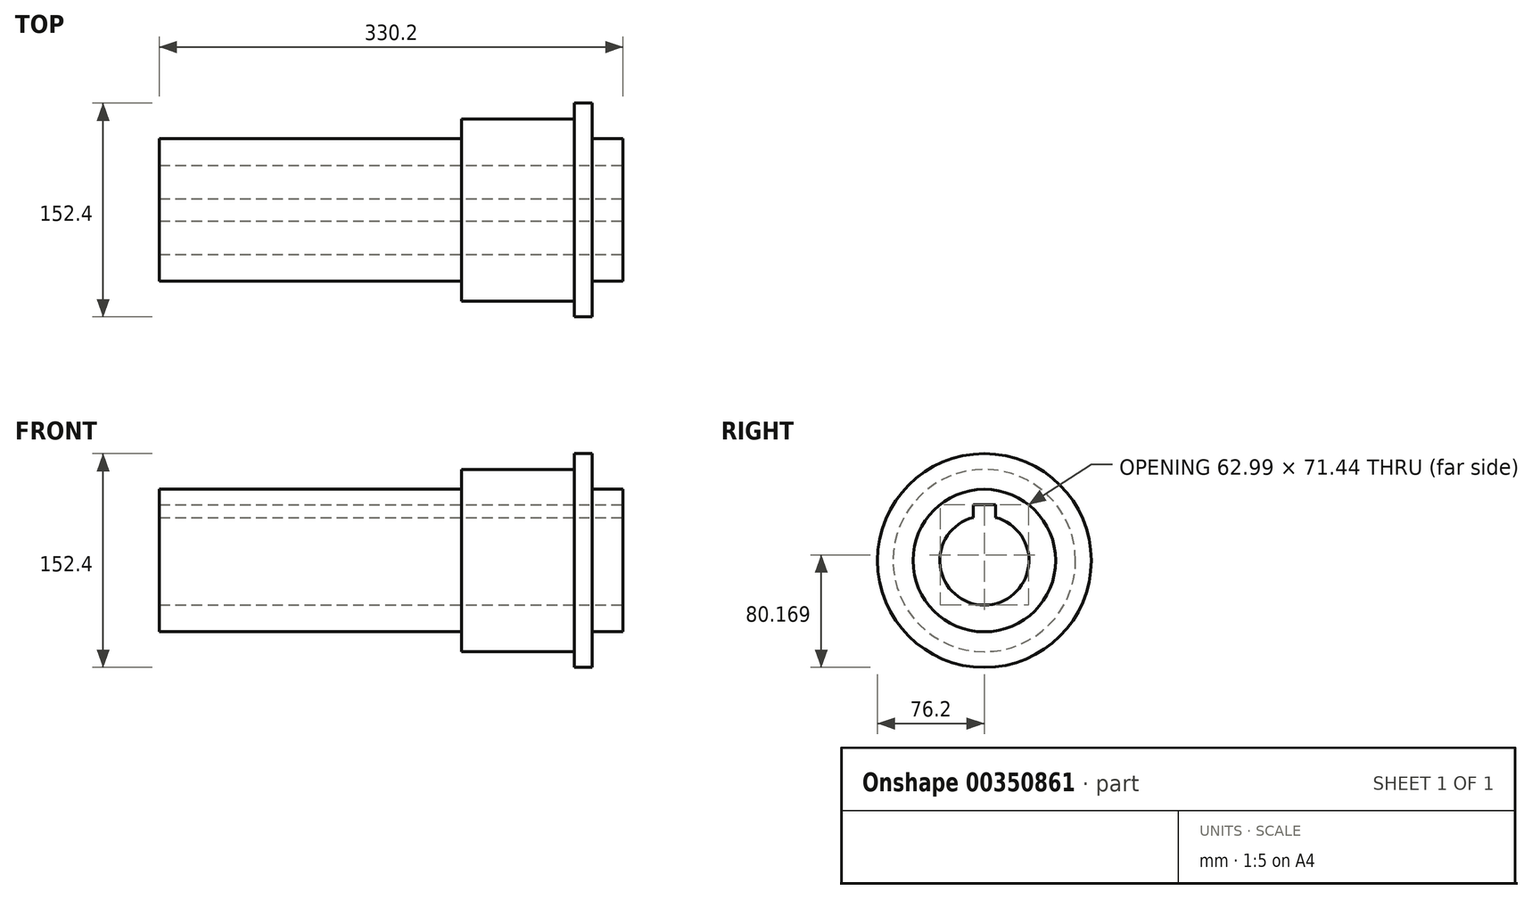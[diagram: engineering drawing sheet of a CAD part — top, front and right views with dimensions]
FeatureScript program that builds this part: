
annotation { "Feature Type Name" : "Feature", "Feature Type Description" : "" }
export const myFeature = defineFeature(function(context is Context, id is Id, definition is map)
    precondition{}
    {
        {
            var Q0;
            Q0=qCreatedBy(makeId("Front.planeOp"),FACE);
            var sketch = newSketch(context, id + "F0", { "sketchPlane" : qUnion([Q0])});
            skLineSegment(sketch, "E0", {"start": v(101.8, 31.75) * mm, "end": v(-228.4, 31.75) * mm});
            skLineSegment(sketch, "E1", {"start": v(101.8, 31.75) * mm, "end": v(101.8, 50.8) * mm});
            skLineSegment(sketch, "E2", {"start": v(101.8, 50.8) * mm, "end": v(-228.4, 50.8) * mm});
            skLineSegment(sketch, "E3", {"start": v(-228.4, 50.8) * mm, "end": v(-228.4, 31.75) * mm});
            skLineSegment(sketch, "E4", {"start": v(79.93, 50.8) * mm, "end": v(79.93, 65) * mm});
            skLineSegment(sketch, "E5", {"start": v(79.93, 65) * mm, "end": v(-13.11, 65) * mm});
            skLineSegment(sketch, "E6", {"start": v(-13.11, 65) * mm, "end": v(-13.11, 50.8) * mm});
            skLineSegment(sketch, "E7", {"start": v(79.93, 65) * mm, "end": v(79.93, 76.2) * mm});
            skLineSegment(sketch, "E8", {"start": v(79.93, 76.2) * mm, "end": v(67.23, 76.2) * mm});
            skLineSegment(sketch, "E9", {"start": v(67.23, 76.2) * mm, "end": v(67.23, 65) * mm});
            skLineSegment(sketch, "E10", {"start": v(75.8, 0) * mm, "end": v(-76.2, 0) * mm});
            skSolve(sketch);
        }
        {
            var Q0;
            Q0 = qSketchRegion(id + "F0", true);
            var Q1;
            Q1=sQuery(id+"F0.wireOp",EDGE,"E10");
            revolve(context, id + "F1", {"entities" : qUnion([Q0]), "axis" : qUnion([Q1]), "revolveType" : RevolveType.FULL});
        }
        {
            var Q0;
            Q0=makeQuery(id+"F1.opRevolve","SWEPT_FACE",FACE,{"disambiguationData":[OSD([sQuery(id+"F0.wireOp",EDGE,"E1")])]});
            var sketch = newSketch(context, id + "F2", { "sketchPlane" : qUnion([Q0])});
            skLineSegment(sketch, "E11.bottom", {"start": v(7.94, 39.69) * mm, "end": v(-7.94, 39.69) * mm});
            skLineSegment(sketch, "E11.top", {"start": v(7.94, 23.81) * mm, "end": v(-7.94, 23.81) * mm});
            skLineSegment(sketch, "E11.left", {"start": v(7.94, 39.69) * mm, "end": v(7.94, 23.81) * mm});
            skLineSegment(sketch, "E11.right", {"start": v(-7.94, 39.69) * mm, "end": v(-7.94, 23.81) * mm});
            skPoint(sketch, "E11.middle", {"position": v(0, 31.75) * mm});
            skSolve(sketch);
        }
        {
            var Q0;
            {var subQ0=sQuery(id+"F2.wireOp",EDGE,"E11.bottom");Q0=makeQuery(id+"F2.imprint","IMPRINT",FACE,{"disambiguationData":[TD([[makeQuery(id+"F2.imprint","IMPRINT",EDGE,{"derivedFrom":subQ0}),1.0]])]});}
            extrude(context, id + "F3", {"entities" : qUnion([Q0]), "operationType" : NewBodyOperationType.REMOVE, "oppositeDirection" : true, "depth" : 330.2 * mm});
        }
    });
